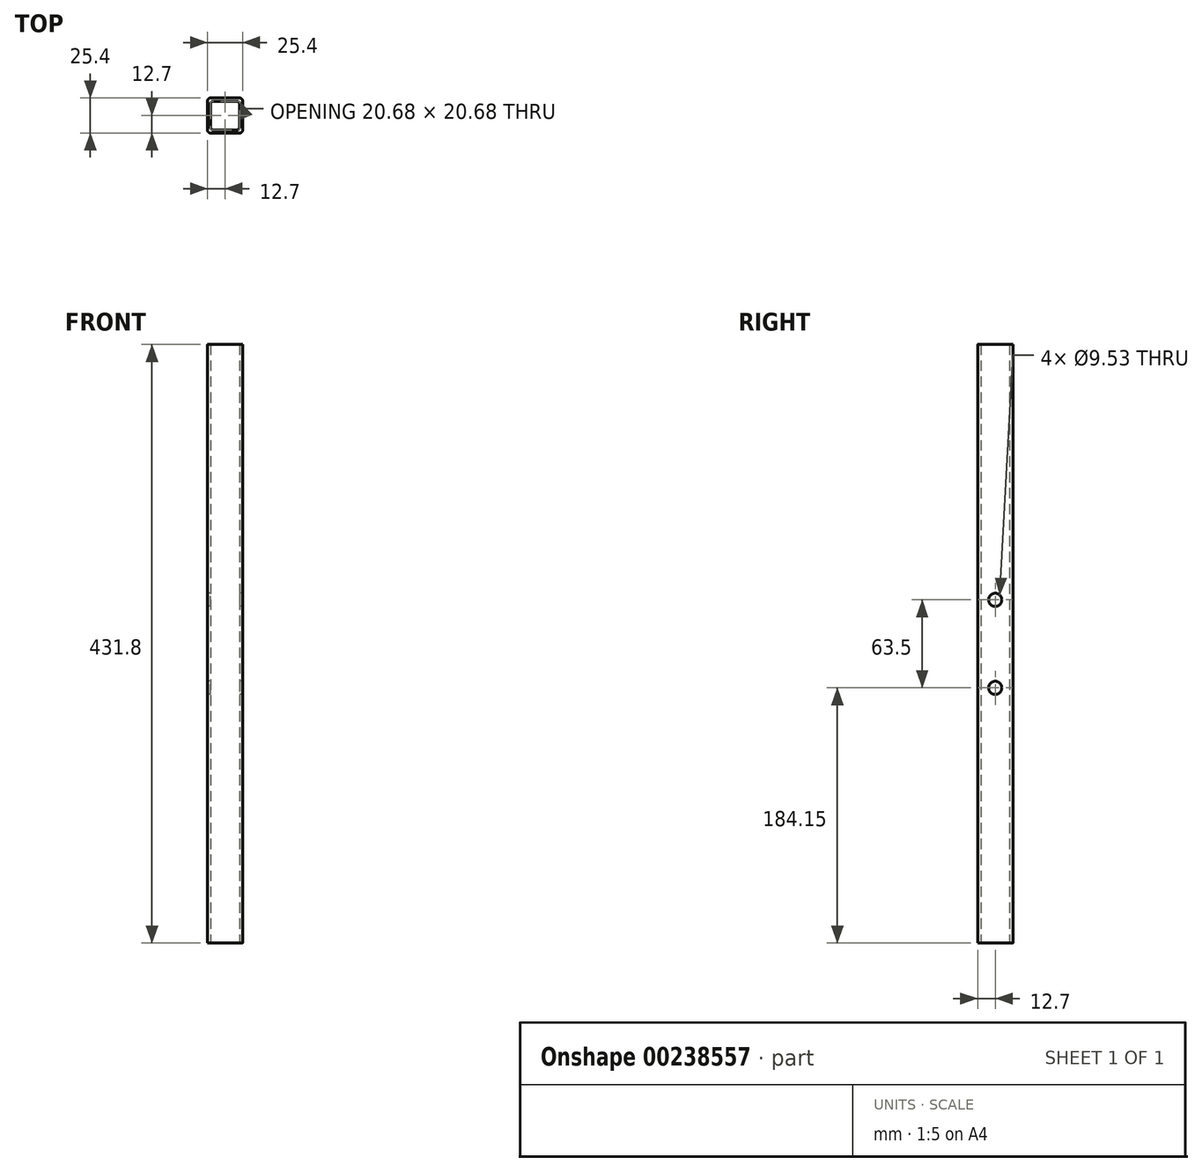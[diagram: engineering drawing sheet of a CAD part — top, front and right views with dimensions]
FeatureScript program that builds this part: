
annotation { "Feature Type Name" : "Feature", "Feature Type Description" : "" }
export const myFeature = defineFeature(function(context is Context, id is Id, definition is map)
    precondition{}
    {
        {
            var Q0;
            Q0=qCreatedBy(makeId("Top.planeOp"),FACE);
            var sketch = newSketch(context, id + "F0", { "sketchPlane" : qUnion([Q0])});
            skLineSegment(sketch, "E0", {"start": v(-12.7, 10.34) * mm, "end": v(-12.7, -10.34) * mm});
            skLineSegment(sketch, "E1", {"start": v(-10.34, -12.7) * mm, "end": v(10.34, -12.7) * mm});
            skLineSegment(sketch, "E2", {"start": v(12.7, -10.34) * mm, "end": v(12.7, 10.34) * mm});
            skLineSegment(sketch, "E3", {"start": v(10.34, 12.7) * mm, "end": v(-10.34, 12.7) * mm});
            skLineSegment(sketch, "E4", {"start": v(0, 12.7) * mm, "end": v(0, -12.7) * mm, "construction": true});
            skLineSegment(sketch, "E5", {"start": v(-12.7, 0) * mm, "end": v(12.7, 0) * mm, "construction": true});
            skPoint(sketch, "E6", {"position": v(0, 0) * mm});
            skPoint(sketch, "E7.visualSharp", {"position": v(-12.7, 12.7) * mm});
            skArc(sketch, "E7.filletArc", {"start": v(-10.34, 12.7) * mm, "mid": v(-12, 12) * mm, "end": v(-12.7, 10.34) * mm});
            skPoint(sketch, "E8.visualSharp", {"position": v(12.7, 12.7) * mm});
            skArc(sketch, "E8.filletArc", {"start": v(12.7, 10.34) * mm, "mid": v(12, 12) * mm, "end": v(10.34, 12.7) * mm});
            skPoint(sketch, "E9.visualSharp", {"position": v(12.7, -12.7) * mm});
            skArc(sketch, "E9.filletArc", {"start": v(10.34, -12.7) * mm, "mid": v(12, -12) * mm, "end": v(12.7, -10.34) * mm});
            skPoint(sketch, "E10.visualSharp", {"position": v(-12.7, -12.7) * mm});
            skArc(sketch, "E10.filletArc", {"start": v(-12.7, -10.34) * mm, "mid": v(-12, -12) * mm, "end": v(-10.34, -12.7) * mm});
            skLineSegment(sketch, "E11.0", {"start": v(8.81, 10.34) * mm, "end": v(-8.81, 10.34) * mm});
            skLineSegment(sketch, "E12.0", {"start": v(10.34, -8.81) * mm, "end": v(10.34, 8.81) * mm});
            skLineSegment(sketch, "E13.0", {"start": v(-8.81, -10.34) * mm, "end": v(8.81, -10.34) * mm});
            skLineSegment(sketch, "E14.0", {"start": v(-10.34, 8.81) * mm, "end": v(-10.34, -8.81) * mm});
            skArc(sketch, "E15.filletArc", {"start": v(-8.81, 10.34) * mm, "mid": v(-9.9, 9.9) * mm, "end": v(-10.34, 8.81) * mm});
            skArc(sketch, "E16.filletArc", {"start": v(10.34, 8.81) * mm, "mid": v(9.9, 9.9) * mm, "end": v(8.81, 10.34) * mm});
            skArc(sketch, "E17.filletArc", {"start": v(8.81, -10.34) * mm, "mid": v(9.9, -9.9) * mm, "end": v(10.34, -8.81) * mm});
            skArc(sketch, "E18.filletArc", {"start": v(-10.34, -8.81) * mm, "mid": v(-9.9, -9.9) * mm, "end": v(-8.81, -10.34) * mm});
            skSolve(sketch);
        }
        {
            var Q0;
            Q0=makeQuery(id+"F0.imprint","IMPRINT",FACE,{"disambiguationData":[TD([[makeQuery(id+"F0.imprint","IMPRINT",EDGE,{"derivedFrom":sQuery(id+"F0.wireOp",EDGE,"E0")}),1.0]])]});
            extrude(context, id + "F1", {"entities" : qUnion([Q0]), "depth" : 431.8 * mm});
        }
        {
            var Q0;
            Q0=makeQuery(id+"F1.opExtrude","SWEPT_FACE",FACE,{"disambiguationData":[OSD([sQuery(id+"F0.wireOp",EDGE,"E2")])]});
            var sketch = newSketch(context, id + "F2", { "sketchPlane" : qUnion([Q0])});
            skPoint(sketch, "E19", {"position": v(0, 247.65) * mm});
            skPoint(sketch, "E20", {"position": v(0, 184.15) * mm});
            skPoint(sketch, "E20.positionSnap0", {"position": v(10.34, 184.15) * mm});
            skSolve(sketch);
        }
        {
            var Q0;
            Q0=sQuery(id+"F2.wireOp",VERTEX,"E19");
            var Q1;
            Q1=sQuery(id+"F2.wireOp",VERTEX,"E20");
            var Q2;
            Q2=makeQuery(id+"F1.opExtrude","SWEPT_BODY",BODY,{"disambiguationData":[OSD([sQuery(id+"F0.wireOp",EDGE,"E0"),sQuery(id+"F0.wireOp",EDGE,"E1"),sQuery(id+"F0.wireOp",EDGE,"E2"),sQuery(id+"F0.wireOp",EDGE,"E3"),sQuery(id+"F0.wireOp",EDGE,"E7.filletArc"),sQuery(id+"F0.wireOp",EDGE,"E8.filletArc"),sQuery(id+"F0.wireOp",EDGE,"E9.filletArc"),sQuery(id+"F0.wireOp",EDGE,"E10.filletArc"),sQuery(id+"F0.wireOp",EDGE,"E11.0"),sQuery(id+"F0.wireOp",EDGE,"E12.0"),sQuery(id+"F0.wireOp",EDGE,"E13.0"),sQuery(id+"F0.wireOp",EDGE,"E14.0"),sQuery(id+"F0.wireOp",EDGE,"E15.filletArc"),sQuery(id+"F0.wireOp",EDGE,"E16.filletArc"),sQuery(id+"F0.wireOp",EDGE,"E17.filletArc"),sQuery(id+"F0.wireOp",EDGE,"E18.filletArc")])]});
            hole(context, id + "F3", {"style" : HoleStyle.SIMPLE, "endStyle" : HoleEndStyle.THROUGH, "holeDiameter" : 9.52 * mm, "locations" : qUnion([Q0, Q1]), "scope" : qUnion([Q2]), "isTappedThrough" : true, "startStyle" : HoleStartStyle.PART});
        }
    });
